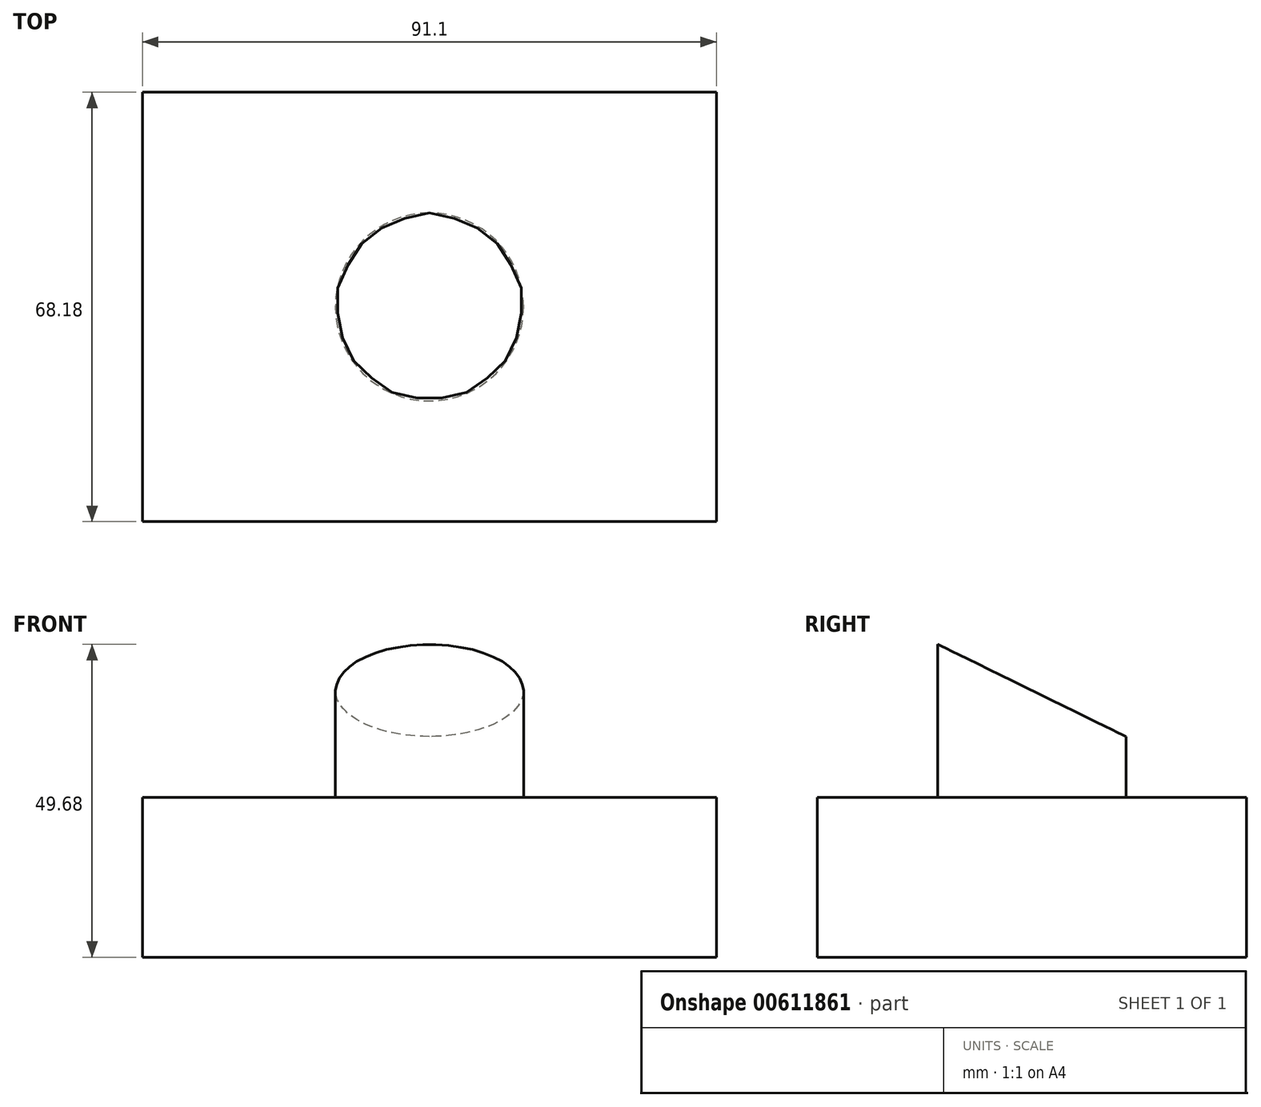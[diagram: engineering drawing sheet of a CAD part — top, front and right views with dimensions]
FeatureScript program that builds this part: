
annotation { "Feature Type Name" : "Feature", "Feature Type Description" : "" }
export const myFeature = defineFeature(function(context is Context, id is Id, definition is map)
    precondition{}
    {
        {
            var Q0;
            Q0=qCreatedBy(makeId("Top.planeOp"),FACE);
            var sketch = newSketch(context, id + "F0", { "sketchPlane" : qUnion([Q0])});
            skLineSegment(sketch, "E0.bottom", {"start": v(45.55, 34.1) * mm, "end": v(-45.55, 34.1) * mm});
            skLineSegment(sketch, "E0.top", {"start": v(45.55, -34.1) * mm, "end": v(-45.55, -34.1) * mm});
            skLineSegment(sketch, "E0.left", {"start": v(45.55, 34.1) * mm, "end": v(45.55, -34.1) * mm});
            skLineSegment(sketch, "E0.right", {"start": v(-45.55, 34.1) * mm, "end": v(-45.55, -34.1) * mm});
            skPoint(sketch, "E0.middle", {"position": v(0, 0) * mm});
            skCircle(sketch, "E1", {"center": v(0, 0) * mm, "radius": 14.93 * mm});
            skSolve(sketch);
        }
        {
            var Q0;
            Q0=makeQuery(id+"F0.imprint","IMPRINT",FACE,{"disambiguationData":[TD([[makeQuery(id+"F0.imprint","IMPRINT",EDGE,{"derivedFrom":sQuery(id+"F0.wireOp",EDGE,"E1")}),1.0]])]});
            extrude(context, id + "F1", {"entities" : qUnion([Q0]), "depth" : 38.1 * mm, "offsetDistance" : 25.4 * mm});
        }
        {
            var Q0;
            Q0=makeQuery(id+"F0.imprint","IMPRINT",FACE,{"disambiguationData":[TD([[makeQuery(id+"F0.imprint","IMPRINT",EDGE,{"derivedFrom":sQuery(id+"F0.wireOp",EDGE,"E0.bottom")}),1.0]])]});
            extrude(context, id + "F2", {"entities" : qUnion([Q0]), "operationType" : NewBodyOperationType.ADD, "depth" : 25.4 * mm, "offsetDistance" : 25.4 * mm});
        }
        {
            var Q0;
            Q0=makeQuery(id+"F1.opExtrude","CAP_FACE",FACE,{"disambiguationData":[OSD([sQuery(id+"F0.wireOp",EDGE,"E1")])],"isStart":false});
            extrude(context, id + "F3", {"entities" : qUnion([Q0]), "operationType" : NewBodyOperationType.ADD, "depth" : 12.7 * mm, "offsetDistance" : 25.4 * mm});
        }
        {
            var Q0;
            Q0=qCreatedBy(makeId("Right.planeOp"),FACE);
            var sketch = newSketch(context, id + "F4", { "sketchPlane" : qUnion([Q0])});
            skLineSegment(sketch, "E2", {"start": v(-16.4, 50.4) * mm, "end": v(20.99, 32.08) * mm});
            skLineSegment(sketch, "E3", {"start": v(20.99, 32.08) * mm, "end": v(20.99, 54.62) * mm});
            skLineSegment(sketch, "E4", {"start": v(20.99, 54.62) * mm, "end": v(-16.59, 54.62) * mm});
            skLineSegment(sketch, "E5", {"start": v(-16.59, 54.62) * mm, "end": v(-16.4, 50.4) * mm});
            skSolve(sketch);
        }
        {
            var Q0;
            Q0=makeQuery(id+"F4.imprint","IMPRINT",FACE,{"disambiguationData":[TD([[makeQuery(id+"F4.imprint","IMPRINT",EDGE,{"derivedFrom":sQuery(id+"F4.wireOp",EDGE,"E2")}),1.0]])]});
            extrude(context, id + "F5", {"entities" : qUnion([Q0]), "operationType" : NewBodyOperationType.REMOVE, "endBound" : BoundingType.SYMMETRIC, "depth" : 50.8 * mm, "offsetDistance" : 25.4 * mm});
        }
    });
